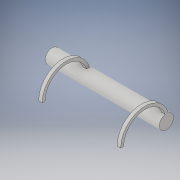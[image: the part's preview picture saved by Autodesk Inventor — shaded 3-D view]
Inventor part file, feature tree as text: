
AUTODESK INVENTOR PART (.ipt)
format: ipt  version: 2017 (Build 210142000, 142)  size: 131,584 bytes
history: native  units: in
note: dims shown in document units (in); Inventor stores cm internally (conversion verified against a paired STEP export)
features: extrude x3, sketch x3, plane x1
ambient origin geometry x8: Origin, YZ Plane, XZ Plane, XY Plane, X Axis, Y Axis, Z Axis, Center Point
bodies: Solid1 (feature_tree)
feature tree (7):
  extrude  "Extrusion1"  Depth=4.0in TaperAngle=0.0deg
  extrude  "Extrusion2"  Depth=0.1in
  plane  "Work Plane1"
  extrude  "Extrusion3"  Depth=0.75in
  sketch  "Sketch1"  dims[d0=0.5in d1=4.0in d2=0.0in]
  sketch  "Sketch2"  dims[d3=0.1in d4=0.1in]
  sketch  "Sketch3"  dims[d5=1.5in d6=0.75in d7=0.125in d8=0.0in d9=-2.75in d10=0.1in d11=0.1in d12=1.5in d13=0.75in d14=180.0deg d15=0.25in d16=0.125in d17=0.0in]
